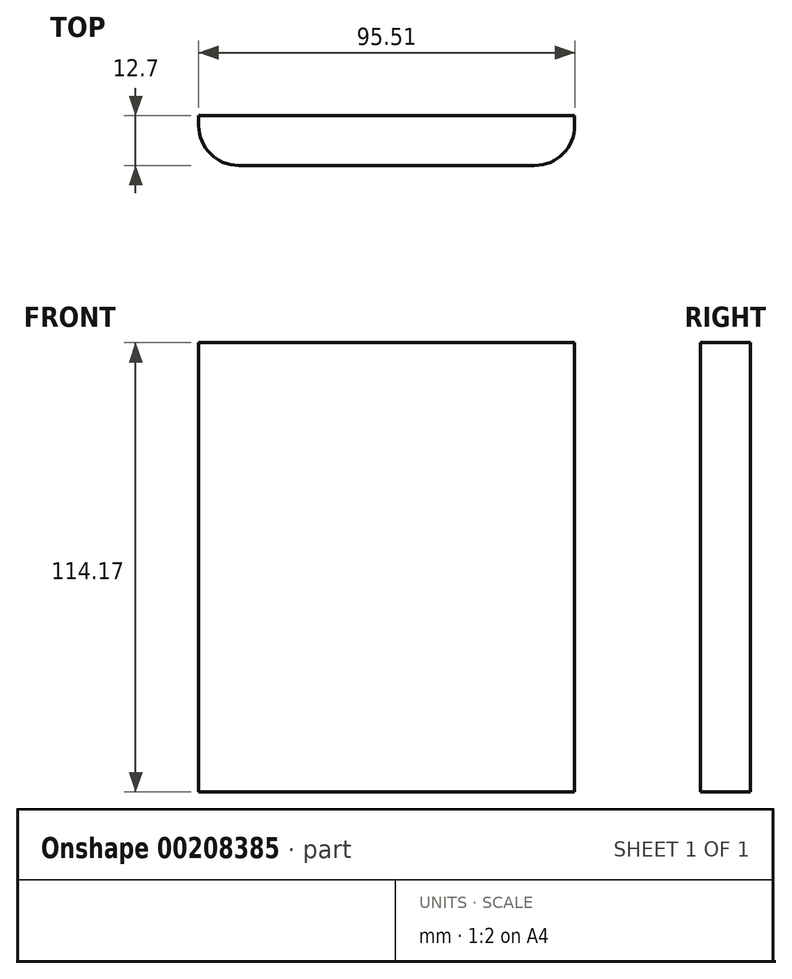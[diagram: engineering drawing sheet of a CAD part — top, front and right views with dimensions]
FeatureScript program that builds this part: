
annotation { "Feature Type Name" : "Feature", "Feature Type Description" : "" }
export const myFeature = defineFeature(function(context is Context, id is Id, definition is map)
    precondition{}
    {
        {
            var Q0;
            Q0=qCreatedBy(makeId("Front.planeOp"),FACE);
            var sketch = newSketch(context, id + "F0", { "sketchPlane" : qUnion([Q0])});
            skLineSegment(sketch, "E0.bottom", {"start": v(-48.19, 44.93) * mm, "end": v(47.32, 44.93) * mm});
            skLineSegment(sketch, "E0.top", {"start": v(-48.19, -69.24) * mm, "end": v(47.32, -69.24) * mm});
            skLineSegment(sketch, "E0.left", {"start": v(-48.19, 44.93) * mm, "end": v(-48.19, -69.24) * mm});
            skLineSegment(sketch, "E0.right", {"start": v(47.32, 44.93) * mm, "end": v(47.32, -69.24) * mm});
            skSolve(sketch);
        }
        {
            var Q0;
            Q0=makeQuery(id+"F0.imprint","IMPRINT",FACE,{"disambiguationData":[TD([[makeQuery(id+"F0.imprint","IMPRINT",EDGE,{"derivedFrom":sQuery(id+"F0.wireOp",EDGE,"E0.bottom")}),-1.0]])]});
            extrude(context, id + "F1", {"entities" : qUnion([Q0]), "depth" : 12.7 * mm});
        }
        {
            var Q0;
            Q0=makeQuery(id+"F1.opExtrude","CAP_EDGE",EDGE,{"disambiguationData":[OSD([sQuery(id+"F0.wireOp",EDGE,"E0.left")])],"isStart":false});
            var Q1;
            Q1=makeQuery(id+"F1.opExtrude","CAP_EDGE",EDGE,{"disambiguationData":[OSD([sQuery(id+"F0.wireOp",EDGE,"E0.right")])],"isStart":false});
            fillet(context, id + "F2", {"entities" : qUnion([Q0, Q1]), "radius" : 10.16 * mm, "tangentPropagation" : true, "allowEdgeOverflow" : false});
        }
    });
